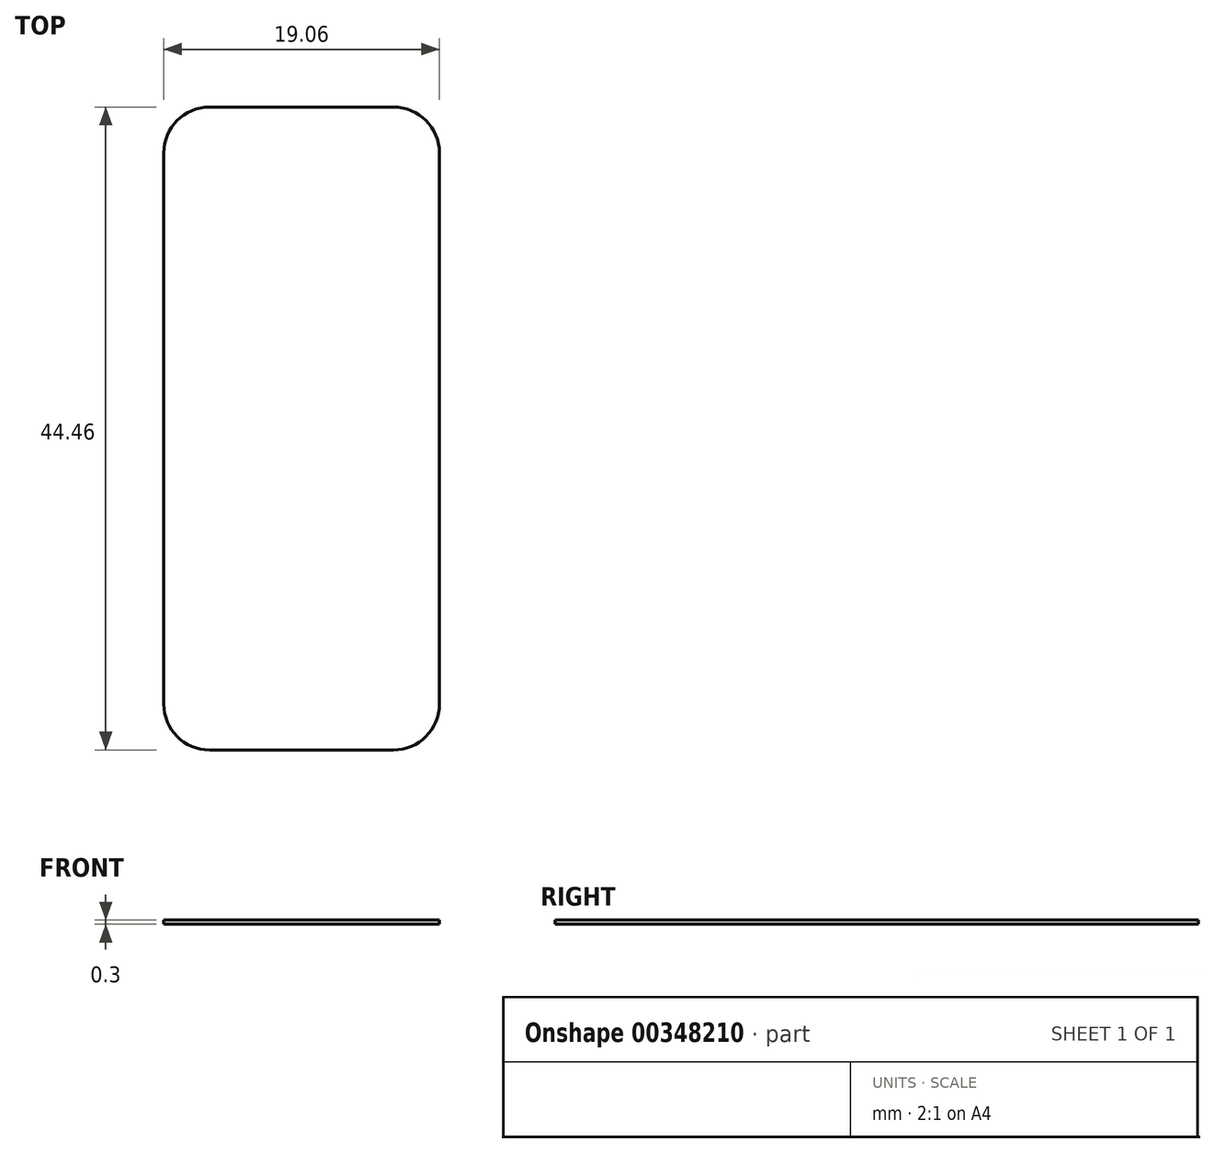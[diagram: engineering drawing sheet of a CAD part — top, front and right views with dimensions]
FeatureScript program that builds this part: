
annotation { "Feature Type Name" : "Feature", "Feature Type Description" : "" }
export const myFeature = defineFeature(function(context is Context, id is Id, definition is map)
    precondition{}
    {
        {
            var Q0;
            Q0=qCreatedBy(makeId("Top.planeOp"),FACE);
            var sketch = newSketch(context, id + "F0", { "sketchPlane" : qUnion([Q0])});
            skLineSegment(sketch, "E0", {"start": v(-9.52, 0) * mm, "end": v(-9.52, 19.05) * mm});
            skLineSegment(sketch, "E1", {"start": v(9.53, 0) * mm, "end": v(9.53, 19.05) * mm});
            skLineSegment(sketch, "E2", {"start": v(-9.52, 0) * mm, "end": v(-9.52, -19.05) * mm});
            skLineSegment(sketch, "E3", {"start": v(9.53, 0) * mm, "end": v(9.53, -19.05) * mm});
            skLineSegment(sketch, "E4", {"start": v(-6.35, 22.23) * mm, "end": v(6.35, 22.23) * mm});
            skLineSegment(sketch, "E5", {"start": v(-6.35, -22.22) * mm, "end": v(6.35, -22.23) * mm});
            skPoint(sketch, "E6.visualSharp", {"position": v(-9.52, 22.22) * mm});
            skArc(sketch, "E6.filletArc", {"start": v(-6.35, 22.22) * mm, "mid": v(-8.6, 21.3) * mm, "end": v(-9.52, 19.05) * mm});
            skPoint(sketch, "E7.visualSharp", {"position": v(9.53, 22.23) * mm});
            skArc(sketch, "E7.filletArc", {"start": v(9.53, 19.05) * mm, "mid": v(8.6, 21.3) * mm, "end": v(6.35, 22.23) * mm});
            skPoint(sketch, "E8.visualSharp", {"position": v(9.53, -22.23) * mm});
            skArc(sketch, "E8.filletArc", {"start": v(6.35, -22.23) * mm, "mid": v(8.6, -21.3) * mm, "end": v(9.53, -19.05) * mm});
            skPoint(sketch, "E9.visualSharp", {"position": v(-9.52, -22.22) * mm});
            skArc(sketch, "E9.filletArc", {"start": v(-9.52, -19.05) * mm, "mid": v(-8.6, -21.3) * mm, "end": v(-6.35, -22.22) * mm});
            skSolve(sketch);
        }
        {
            var Q0;
            Q0 = qSketchRegion(id + "F0", true);
            extrude(context, id + "F1", {"entities" : qUnion([Q0]), "depth" : 0.3 * mm, "offsetDistance" : 25.4 * mm});
        }
    });
